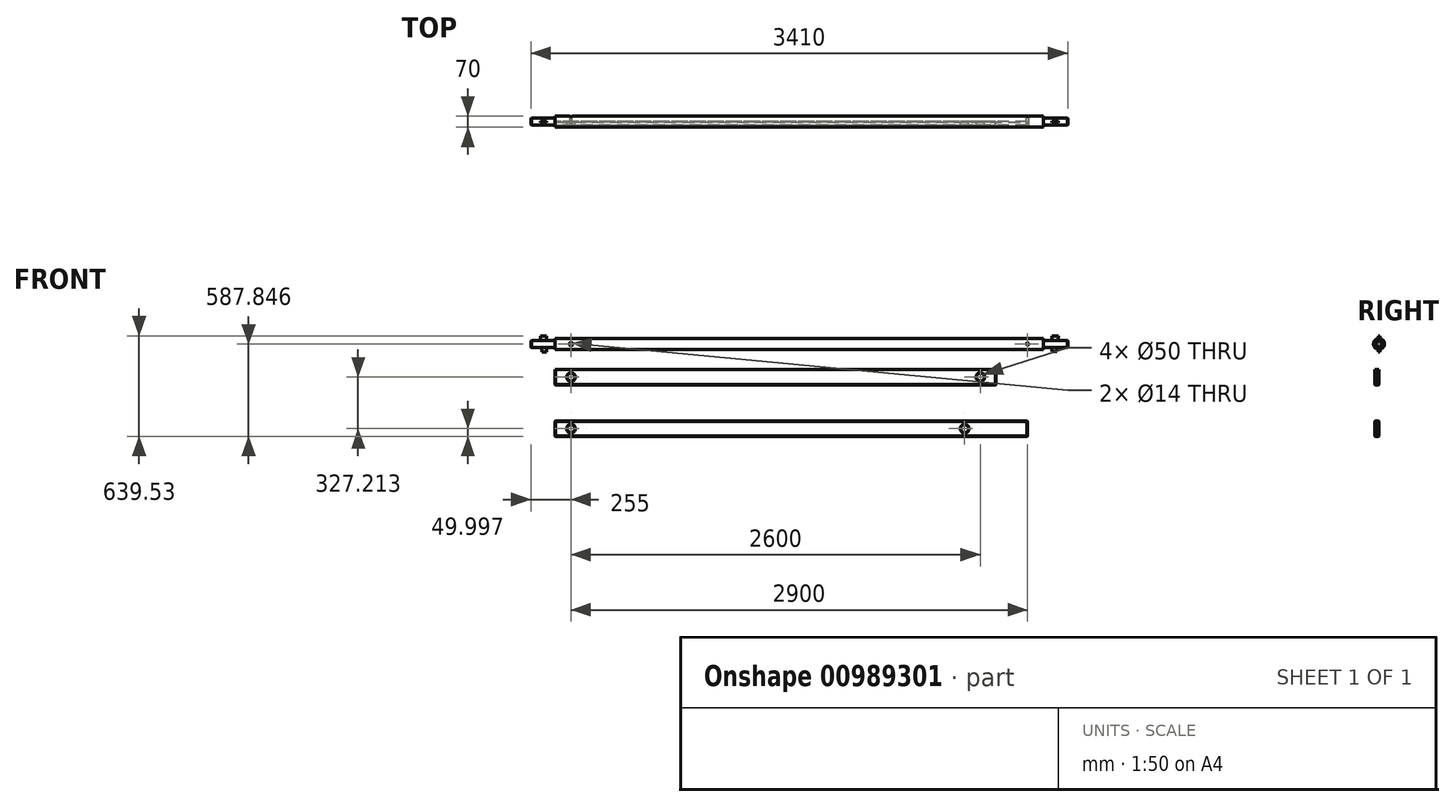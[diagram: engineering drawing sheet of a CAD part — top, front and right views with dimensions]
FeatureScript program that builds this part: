
annotation { "Feature Type Name" : "Feature", "Feature Type Description" : "" }
export const myFeature = defineFeature(function(context is Context, id is Id, definition is map)
    precondition{}
    {
        {
            var Q0;
            Q0=qCreatedBy(makeId("Front.planeOp"),FACE);
            var sketch = newSketch(context, id + "F0", { "sketchPlane" : qUnion([Q0])});
            skLineSegment(sketch, "E0", {"start": v(0, 0) * mm, "end": v(2800, 0) * mm});
            skLineSegment(sketch, "E1", {"start": v(0, 100) * mm, "end": v(2800, 100) * mm});
            skLineSegment(sketch, "E2", {"start": v(2800, 100) * mm, "end": v(2800, 0) * mm});
            skLineSegment(sketch, "E3", {"start": v(0, 0) * mm, "end": v(0, 100) * mm});
            skCircle(sketch, "E4", {"center": v(100, 50) * mm, "radius": 25 * mm});
            skLineSegment(sketch, "E5", {"start": v(0, 50) * mm, "end": v(100, 50) * mm});
            skLineSegment(sketch, "E6", {"start": v(2800, 50) * mm, "end": v(2700, 50) * mm});
            skCircle(sketch, "E7", {"center": v(2700, 50) * mm, "radius": 25 * mm});
            skSolve(sketch);
        }
        {
            var Q0;
            {var subQ1=sQuery(id+"F0.wireOp",EDGE,"E3");var subQ7=sQuery(id+"F0.wireOp",EDGE,"E1");var subQ8=makeQuery(id+"F0.imprint","INTERSECT",VERTEX,{"derivedFrom":[subQ7,subQ1]});Q0=makeQuery(id+"F0.imprint","IMPRINT",FACE,{"disambiguationData":[TD([[makeQuery(id+"F0.imprint","IMPRINT",EDGE,{"disambiguationData":[TD([[subQ8,-1.0]])],"derivedFrom":subQ7}),-1.0]])]});}
            var Q1;
            {var subQ1=sQuery(id+"F0.wireOp",EDGE,"E0");Q1=makeQuery(id+"F0.imprint","IMPRINT",FACE,{"disambiguationData":[TD([[makeQuery(id+"F0.imprint","IMPRINT",EDGE,{"derivedFrom":subQ1}),1.0]])]});}
            var Q2;
            {var subQ1=sQuery(id+"F0.wireOp",EDGE,"E1");var subQ6=sQuery(id+"F0.wireOp",EDGE,"E2");var subQ9=makeQuery(id+"F0.imprint","INTERSECT",VERTEX,{"derivedFrom":[subQ1,subQ6]});Q2=makeQuery(id+"F0.imprint","IMPRINT",FACE,{"disambiguationData":[TD([[makeQuery(id+"F0.imprint","IMPRINT",EDGE,{"disambiguationData":[TD([[subQ9,1.0]])],"derivedFrom":subQ1}),-1.0]])]});}
            extrude(context, id + "F1", {"entities" : qUnion([Q0, Q1, Q2]), "depth" : 25 * mm, "offsetDistance" : 25 * mm});
        }
        {
            var Q0;
            Q0=qCreatedBy(makeId("Front.planeOp"),FACE);
            var sketch = newSketch(context, id + "F2", { "sketchPlane" : qUnion([Q0])});
            skLineSegment(sketch, "E8", {"start": v(0, -327.21) * mm, "end": v(2700, -327.21) * mm});
            skLineSegment(sketch, "E9", {"start": v(0, -227.21) * mm, "end": v(2700, -227.21) * mm});
            skLineSegment(sketch, "E10", {"start": v(2700, -227.21) * mm, "end": v(2700, -327.21) * mm});
            skLineSegment(sketch, "E11", {"start": v(0, -327.21) * mm, "end": v(0, -227.21) * mm});
            skCircle(sketch, "E12", {"center": v(100, -277.21) * mm, "radius": 25 * mm});
            skLineSegment(sketch, "E13", {"start": v(0, -277.21) * mm, "end": v(100, -277.21) * mm});
            skLineSegment(sketch, "E14", {"start": v(2700, -277.21) * mm, "end": v(2600, -277.21) * mm});
            skCircle(sketch, "E15", {"center": v(2600, -277.21) * mm, "radius": 25 * mm});
            skLineSegment(sketch, "E16.bottom", {"start": v(2700, -227.21) * mm, "end": v(3000, -227.21) * mm});
            skLineSegment(sketch, "E16.top", {"start": v(2700, -327.21) * mm, "end": v(3000, -327.21) * mm});
            skLineSegment(sketch, "E16.right", {"start": v(3000, -227.21) * mm, "end": v(3000, -327.21) * mm});
            skSolve(sketch);
        }
        {
            var Q0;
            {var subQ1=sQuery(id+"F2.wireOp",EDGE,"E11");var subQ5=sQuery(id+"F2.wireOp",EDGE,"E9");var subQ6=makeQuery(id+"F2.imprint","INTERSECT",VERTEX,{"derivedFrom":[subQ5,subQ1]});Q0=makeQuery(id+"F2.imprint","IMPRINT",FACE,{"disambiguationData":[TD([[makeQuery(id+"F2.imprint","IMPRINT",EDGE,{"disambiguationData":[TD([[subQ6,-1.0]])],"derivedFrom":subQ5}),-1.0]])]});}
            var Q1;
            {var subQ1=sQuery(id+"F2.wireOp",EDGE,"E8");Q1=makeQuery(id+"F2.imprint","IMPRINT",FACE,{"disambiguationData":[TD([[makeQuery(id+"F2.imprint","IMPRINT",EDGE,{"derivedFrom":subQ1}),1.0]])]});}
            var Q2;
            {var subQ1=sQuery(id+"F2.wireOp",EDGE,"E14");var subQ7=sQuery(id+"F2.wireOp",EDGE,"E10");var subQ8=makeQuery(id+"F2.imprint","INTERSECT",VERTEX,{"derivedFrom":[subQ1,subQ7]});Q2=makeQuery(id+"F2.imprint","IMPRINT",FACE,{"disambiguationData":[TD([[makeQuery(id+"F2.imprint","IMPRINT",EDGE,{"disambiguationData":[TD([[subQ8,-1.0]])],"derivedFrom":subQ1}),-1.0]])]});}
            var Q3;
            {var subQ3=sQuery(id+"F2.wireOp",EDGE,"E16.bottom");Q3=makeQuery(id+"F2.imprint","IMPRINT",FACE,{"disambiguationData":[TD([[makeQuery(id+"F2.imprint","IMPRINT",EDGE,{"derivedFrom":subQ3}),-1.0]])]});}
            extrude(context, id + "F3", {"entities" : qUnion([Q0, Q1, Q2, Q3]), "depth" : 25 * mm, "offsetDistance" : 25 * mm});
        }
        {
            var Q0;
            Q0=qCreatedBy(makeId("Right.planeOp"),FACE);
            var sketch = newSketch(context, id + "F4", { "sketchPlane" : qUnion([Q0])});
            skCircle(sketch, "E17", {"center": v(0, 260.58) * mm, "radius": 22.5 * mm});
            skCircle(sketch, "E18", {"center": v(0, 260.58) * mm, "radius": 35 * mm});
            skSolve(sketch);
        }
        {
            var Q0;
            Q0=makeQuery(id+"F4.imprint","IMPRINT",FACE,{"disambiguationData":[TD([[makeQuery(id+"F4.imprint","IMPRINT",EDGE,{"derivedFrom":sQuery(id+"F4.wireOp",EDGE,"E17")}),1.0]])]});
            extrude(context, id + "F5", {"entities" : qUnion([Q0]), "depth" : -155 * mm, "offsetDistance" : 25 * mm});
        }
        {
            var Q0;
            Q0=makeQuery(id+"F5.opExtrude","CAP_FACE",FACE,{"disambiguationData":[OSD([sQuery(id+"F4.wireOp",EDGE,"E17")])],"isStart":true});
            extrude(context, id + "F6", {"entities" : qUnion([Q0]), "operationType" : NewBodyOperationType.ADD, "depth" : 3255 * mm, "offsetDistance" : 25 * mm});
        }
        {
            var Q0;
            Q0 = qSketchRegion(id + "F4", true);
            extrude(context, id + "F7", {"entities" : qUnion([Q0]), "operationType" : NewBodyOperationType.ADD, "depth" : 3100 * mm, "offsetDistance" : 25 * mm});
        }
        {
            var Q0;
            Q0=qCreatedBy(makeId("Front.planeOp"),FACE);
            var sketch = newSketch(context, id + "F8", { "sketchPlane" : qUnion([Q0])});
            skLineSegment(sketch, "E19", {"start": v(-55, 310.64) * mm, "end": v(-55, 210.64) * mm});
            skLineSegment(sketch, "E20", {"start": v(-55, 210.64) * mm, "end": v(-85, 210.64) * mm});
            skLineSegment(sketch, "E21", {"start": v(-85, 210.64) * mm, "end": v(-95, 310.64) * mm});
            skLineSegment(sketch, "E22", {"start": v(-95, 310.64) * mm, "end": v(-55, 310.64) * mm});
            skLineSegment(sketch, "E23", {"start": v(3195, 312.32) * mm, "end": v(3185, 212.32) * mm});
            skLineSegment(sketch, "E24", {"start": v(3185, 212.32) * mm, "end": v(3155, 212.32) * mm});
            skLineSegment(sketch, "E25", {"start": v(3155, 212.32) * mm, "end": v(3155, 312.32) * mm});
            skLineSegment(sketch, "E26", {"start": v(3155, 312.32) * mm, "end": v(3195, 312.32) * mm});
            skSolve(sketch);
        }
        {
            var Q0;
            Q0 = qSketchRegion(id + "F8", true);
            extrude(context, id + "F9", {"entities" : qUnion([Q0]), "operationType" : NewBodyOperationType.ADD, "endBound" : BoundingType.SYMMETRIC, "depth" : 10 * mm, "offsetDistance" : 25 * mm});
        }
        {
            var Q0;
            {var subQ0=sQuery(id+"F8.wireOp",EDGE,"E19");var subQ1=sQuery(id+"F8.wireOp",EDGE,"E21");var subQ3=sQuery(id+"F8.wireOp",EDGE,"E22");Q0=makeQuery(id+"F9.boolean.opBoolean","SPLIT",FACE,{"disambiguationData":[TD([makeQuery(id+"F9.opExtrude","SWEPT_FACE",FACE,{"disambiguationData":[OSD([subQ3])]})])],"derivedFrom":makeQuery(id+"F9.opExtrude","CAP_FACE",FACE,{"disambiguationData":[OSD([subQ0,sQuery(id+"F8.wireOp",EDGE,"E20"),subQ1,subQ3])],"isStart":false})});}
            var sketch = newSketch(context, id + "F10", { "sketchPlane" : qUnion([Q0])});
            skLineSegment(sketch, "E27", {"start": v(-55, 310.64) * mm, "end": v(-19.96, 260.64) * mm});
            skLineSegment(sketch, "E28", {"start": v(-19.96, 260.64) * mm, "end": v(-55, 210.64) * mm});
            skLineSegment(sketch, "E29", {"start": v(-19.96, 260.64) * mm, "end": v(0, 260.64) * mm});
            skLineSegment(sketch, "E30", {"start": v(0, 260.64) * mm, "end": v(100, 260.64) * mm});
            skCircle(sketch, "E31", {"center": v(100, 260.64) * mm, "radius": 7 * mm});
            skLineSegment(sketch, "E32", {"start": v(100, 260.64) * mm, "end": v(3000, 260.64) * mm});
            skCircle(sketch, "E33", {"center": v(3000, 260.64) * mm, "radius": 7 * mm});
            skSolve(sketch);
        }
        {
            var Q0;
            Q0 = qSketchRegion(id + "F10", true);
            extrude(context, id + "F11", {"entities" : qUnion([Q0]), "operationType" : NewBodyOperationType.REMOVE, "endBound" : BoundingType.SYMMETRIC, "depth" : 100 * mm, "offsetDistance" : 25 * mm});
        }
        {
            var Q0;
            Q0=makeQuery(id+"F1.opExtrude","SWEPT_EDGE",EDGE,{"disambiguationData":[OSD([sQuery(id+"F0.wireOp",EDGE,"E1"),sQuery(id+"F0.wireOp",EDGE,"E3")])]});
            var Q1;
            Q1=makeQuery(id+"F1.opExtrude","CAP_EDGE",EDGE,{"disambiguationData":[OSD([sQuery(id+"F0.wireOp",EDGE,"E1")])],"isStart":false});
            var Q2;
            Q2=makeQuery(id+"F1.opExtrude","CAP_FACE",FACE,{"disambiguationData":[OSD([sQuery(id+"F0.wireOp",EDGE,"E0"),sQuery(id+"F0.wireOp",EDGE,"E1"),sQuery(id+"F0.wireOp",EDGE,"E2"),sQuery(id+"F0.wireOp",EDGE,"E3"),sQuery(id+"F0.wireOp",EDGE,"E4"),sQuery(id+"F0.wireOp",EDGE,"E7")])],"isStart":false});
            var Q3;
            Q3=makeQuery(id+"F1.opExtrude","CAP_FACE",FACE,{"disambiguationData":[OSD([sQuery(id+"F0.wireOp",EDGE,"E0"),sQuery(id+"F0.wireOp",EDGE,"E1"),sQuery(id+"F0.wireOp",EDGE,"E2"),sQuery(id+"F0.wireOp",EDGE,"E3"),sQuery(id+"F0.wireOp",EDGE,"E4"),sQuery(id+"F0.wireOp",EDGE,"E7")])],"isStart":true});
            var Q4;
            Q4=makeQuery(id+"F1.opExtrude","SWEPT_FACE",FACE,{"disambiguationData":[OSD([sQuery(id+"F0.wireOp",EDGE,"E3")])]});
            var Q5;
            Q5=makeQuery(id+"F1.opExtrude","SWEPT_FACE",FACE,{"disambiguationData":[OSD([sQuery(id+"F0.wireOp",EDGE,"E2")])]});
            var Q6;
            Q6=makeQuery(id+"F3.opExtrude","SWEPT_FACE",FACE,{"disambiguationData":[OSD([sQuery(id+"F2.wireOp",EDGE,"E16.right")])]});
            var Q7;
            Q7=makeQuery(id+"F3.opExtrude","CAP_FACE",FACE,{"disambiguationData":[OSD([sQuery(id+"F2.wireOp",EDGE,"E8"),sQuery(id+"F2.wireOp",EDGE,"E9"),sQuery(id+"F2.wireOp",EDGE,"E11"),sQuery(id+"F2.wireOp",EDGE,"E12"),sQuery(id+"F2.wireOp",EDGE,"E15"),sQuery(id+"F2.wireOp",EDGE,"E16.bottom"),sQuery(id+"F2.wireOp",EDGE,"E16.top"),sQuery(id+"F2.wireOp",EDGE,"E16.right")])],"isStart":false});
            var Q8;
            Q8=makeQuery(id+"F3.opExtrude","CAP_FACE",FACE,{"disambiguationData":[OSD([sQuery(id+"F2.wireOp",EDGE,"E8"),sQuery(id+"F2.wireOp",EDGE,"E9"),sQuery(id+"F2.wireOp",EDGE,"E11"),sQuery(id+"F2.wireOp",EDGE,"E12"),sQuery(id+"F2.wireOp",EDGE,"E15"),sQuery(id+"F2.wireOp",EDGE,"E16.bottom"),sQuery(id+"F2.wireOp",EDGE,"E16.top"),sQuery(id+"F2.wireOp",EDGE,"E16.right")])],"isStart":true});
            var Q9;
            Q9=makeQuery(id+"F3.opExtrude","SWEPT_FACE",FACE,{"disambiguationData":[OSD([sQuery(id+"F2.wireOp",EDGE,"E11")])]});
            var Q10;
            Q10=makeQuery(id+"F5.opExtrude","CAP_FACE",FACE,{"disambiguationData":[OSD([sQuery(id+"F4.wireOp",EDGE,"E17")])],"isStart":false});
            var Q11;
            Q11=makeQuery(id+"F6.opExtrude","CAP_EDGE",EDGE,{"disambiguationData":[OSD([sQuery(id+"F4.wireOp",EDGE,"E17")])],"isStart":false});
            var Q12;
            Q12=makeQuery(id+"F11.boolean.opBoolean","COPY",FACE,{"derivedFrom":makeQuery(id+"F11.opExtrude","SWEPT_FACE",FACE,{"disambiguationData":[OSD([sQuery(id+"F10.wireOp",EDGE,"E31")])]})});
            chamfer(context, id + "F12", {"entities" : qUnion([Q0, Q1, Q2, Q3, Q4, Q5, Q6, Q7, Q8, Q9, Q10, Q11, Q12]), "width" : 3 * mm, "tangentPropagation" : true});
        }
    });
